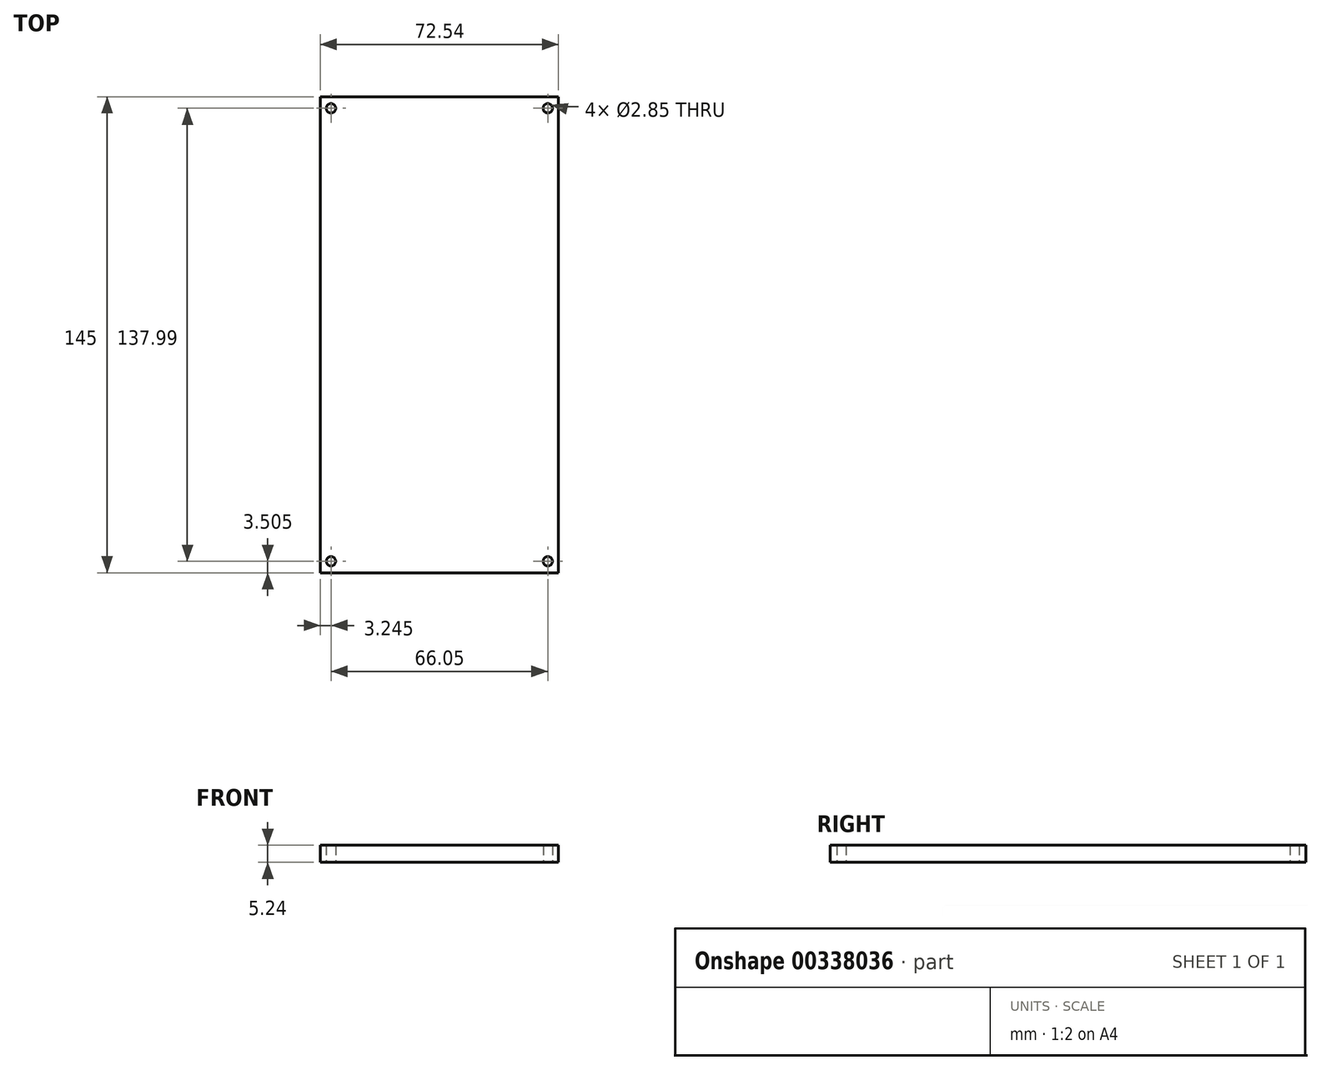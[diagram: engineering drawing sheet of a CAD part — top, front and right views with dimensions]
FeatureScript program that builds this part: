
annotation { "Feature Type Name" : "Feature", "Feature Type Description" : "" }
export const myFeature = defineFeature(function(context is Context, id is Id, definition is map)
    precondition{}
    {
        {
            var Q0;
            Q0=qCreatedBy(makeId("Top.planeOp"),FACE);
            var sketch = newSketch(context, id + "F0", { "sketchPlane" : qUnion([Q0])});
            skLineSegment(sketch, "E0.bottom", {"start": v(-36.27, -72.5) * mm, "end": v(-36.27, 72.5) * mm});
            skLineSegment(sketch, "E0.top", {"start": v(36.27, -72.5) * mm, "end": v(36.27, 72.5) * mm});
            skLineSegment(sketch, "E0.left", {"start": v(-36.27, -72.5) * mm, "end": v(36.27, -72.5) * mm});
            skLineSegment(sketch, "E0.right", {"start": v(-36.27, 72.5) * mm, "end": v(36.27, 72.5) * mm});
            skPoint(sketch, "E1", {"position": v(0, 72.5) * mm});
            skPoint(sketch, "E2", {"position": v(36.27, 0) * mm});
            skCircle(sketch, "E3", {"center": v(33.03, 69) * mm, "radius": 1.43 * mm});
            skCircle(sketch, "E4", {"center": v(-33.03, 69) * mm, "radius": 1.43 * mm});
            skCircle(sketch, "E5", {"center": v(33.03, -69) * mm, "radius": 1.43 * mm});
            skCircle(sketch, "E6", {"center": v(-33.03, -69) * mm, "radius": 1.43 * mm});
            skSolve(sketch);
        }
        {
            var Q0;
            Q0 = qSketchRegion(id + "F0", true);
            extrude(context, id + "F1", {"entities" : qUnion([Q0]), "endBound" : BoundingType.SYMMETRIC, "depth" : 5.24 * mm, "offsetDistance" : 25 * mm});
        }
    });
